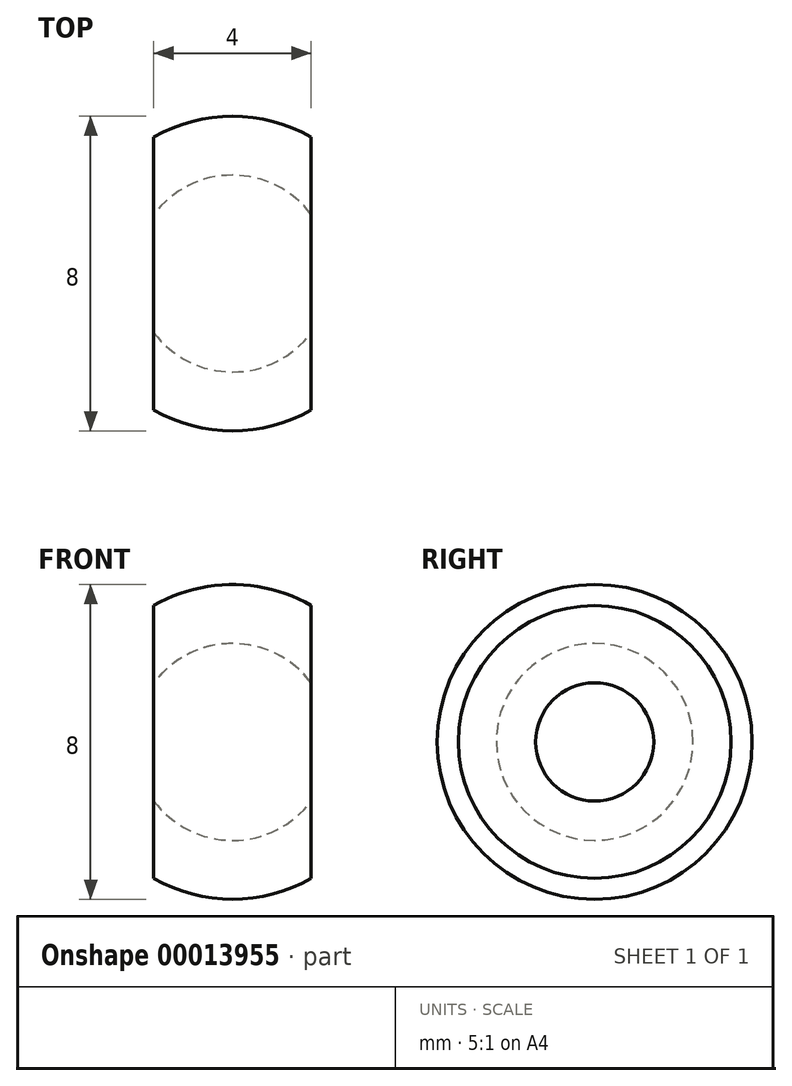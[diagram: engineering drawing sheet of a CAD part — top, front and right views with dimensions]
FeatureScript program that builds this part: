
annotation { "Feature Type Name" : "Feature", "Feature Type Description" : "" }
export const myFeature = defineFeature(function(context is Context, id is Id, definition is map)
    precondition{}
    {
        {
            var Q0;
            Q0=qCreatedBy(makeId("Front.planeOp"),FACE);
            var sketch = newSketch(context, id + "F0", { "sketchPlane" : qUnion([Q0])});
            skArc(sketch, "E0", {"start": v(2.5, 0) * mm, "mid": v(0, 2.5) * mm, "end": v(-2.5, 0) * mm});
            skArc(sketch, "E1", {"start": v(4, 0) * mm, "mid": v(0, 4) * mm, "end": v(-4, 0) * mm});
            skLineSegment(sketch, "E2", {"start": v(-4, 0) * mm, "end": v(-2.5, 0) * mm});
            skLineSegment(sketch, "E3.trimOffspring", {"start": v(2.5, 0) * mm, "end": v(4, 0) * mm});
            skSolve(sketch);
        }
        {
            var Q0;
            Q0=makeQuery(id+"F0.imprint","IMPRINT",FACE,{"disambiguationData":[TD([[makeQuery(id+"F0.imprint","IMPRINT",EDGE,{"derivedFrom":sQuery(id+"F0.wireOp",EDGE,"E0")}),-1.0]])]});
            var Q1;
            Q1=sQuery(id+"F0.wireOp",EDGE,"E3.trimOffspring");
            revolve(context, id + "F1", {"entities" : qUnion([Q0]), "axis" : qUnion([Q1]), "revolveType" : RevolveType.FULL});
        }
        {
            var Q0;
            Q0=qCreatedBy(makeId("Front.planeOp"),FACE);
            var sketch = newSketch(context, id + "F2", { "sketchPlane" : qUnion([Q0])});
            skArc(sketch, "E4", {"start": v(2, -3.46) * mm, "mid": v(4, 0) * mm, "end": v(2, 3.46) * mm});
            skLineSegment(sketch, "E5.left", {"start": v(-2, 3.46) * mm, "end": v(-2, -3.46) * mm});
            skLineSegment(sketch, "E5.right", {"start": v(2, 3.46) * mm, "end": v(2, -3.46) * mm});
            skArc(sketch, "E6.trimOffspring", {"start": v(-2, 3.46) * mm, "mid": v(-4, 0) * mm, "end": v(-2, -3.46) * mm});
            skLineSegment(sketch, "E7", {"start": v(-2, 0) * mm, "end": v(2, 0) * mm, "construction": true});
            skSolve(sketch);
        }
        {
            var Q0;
            Q0 = qSketchRegion(id + "F2", true);
            extrude(context, id + "F3", {"entities" : qUnion([Q0]), "operationType" : NewBodyOperationType.REMOVE, "oppositeDirection" : true, "depth" : 25 * mm, "symmetric" : true});
        }
    });
